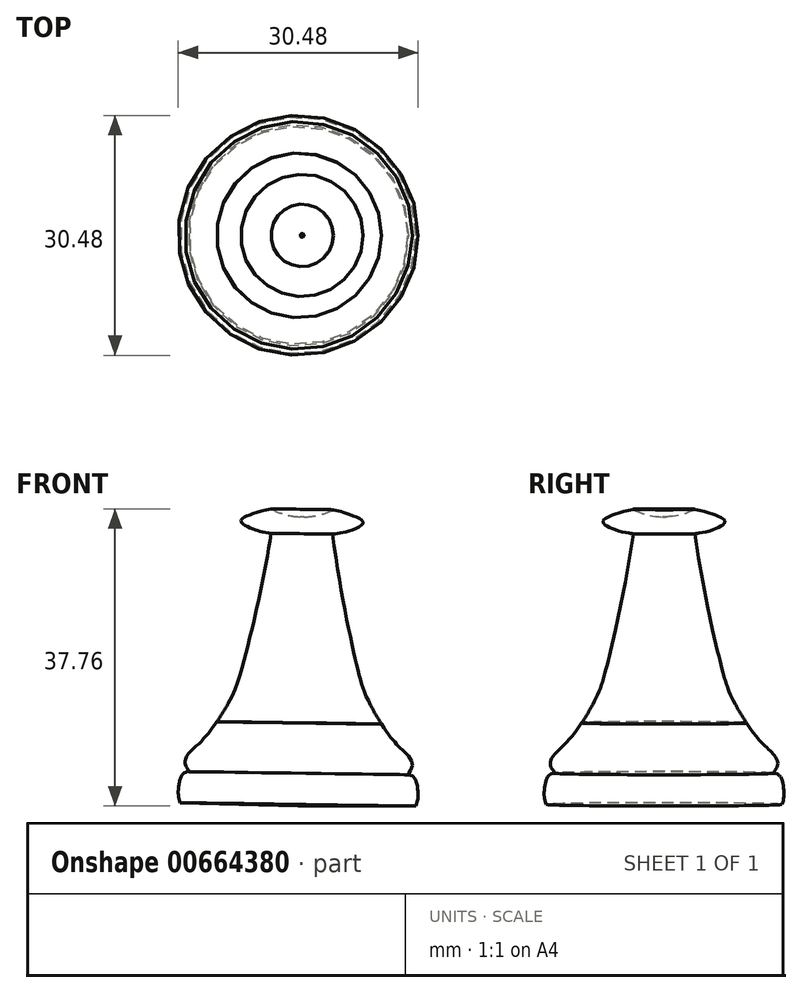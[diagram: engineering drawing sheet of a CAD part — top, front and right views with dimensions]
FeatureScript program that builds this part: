
annotation { "Feature Type Name" : "Feature", "Feature Type Description" : "" }
export const myFeature = defineFeature(function(context is Context, id is Id, definition is map)
    precondition{}
    {
        {
            var Q0;
            Q0=qCreatedBy(makeId("Front.planeOp"),FACE);
            var sketch = newSketch(context, id + "F0", { "sketchPlane" : qUnion([Q0])});
            skArc(sketch, "E0", {"start": v(-3.17, 17.76) * mm, "mid": v(1.07, 26.98) * mm, "end": v(-6.9, 33.26) * mm});
            skFitSpline(sketch, "E1", {"points": [v(-3.17, 17.76) * mm, v(-1.24, 17.2) * mm, v(0.61, 16.13) * mm, v(-1.32, 15.01) * mm, v(-3.28, 14.66) * mm], "startDerivative": vector(7.23, -1.58) * mm, "endDerivative": vector(-7.42, -0.73) * mm});
            skFitSpline(sketch, "E2", {"points": [v(6.36, -15.9) * mm, v(7.55, -17.9) * mm, v(7.34, -19.89) * mm], "startDerivative": vector(6.2, -0.64) * mm, "endDerivative": vector(-2.05, -6.68) * mm});
            skLineSegment(sketch, "E3", {"start": v(-7.66, -19.89) * mm, "end": v(7.34, -19.89) * mm});
            skLineSegment(sketch, "E4", {"start": v(-6.9, 33.26) * mm, "end": v(-7.66, -19.89) * mm});
            skFitSpline(sketch, "E5", {"points": [v(6.36, -15.9) * mm, v(6.33, -15.95) * mm, v(6.82, -14.97) * mm, v(5.9, -13.07) * mm, v(4.06, -11.07) * mm, v(1.14, -6.22) * mm, v(-0.14, -2.21) * mm, v(-3.28, 14.66) * mm], "startDerivative": vector(21.6, 3.05) * mm, "endDerivative": vector(-8.8, 68.35) * mm});
            skFitSpline(sketch, "E6", {"points": [v(2.96, -9.48) * mm, v(2.93, -9.15) * mm, v(2.85, -8.77) * mm, v(2.3, -8.2) * mm, v(1.57, -7.08) * mm], "startDerivative": vector(-0.97, 1.1) * mm, "endDerivative": vector(-0.91, 1.4) * mm});
            skSolve(sketch);
        }
        {
            var Q0;
            Q0=makeQuery(id+"F0.imprint","IMPRINT",FACE,{"disambiguationData":[TD([[makeQuery(id+"F0.imprint","IMPRINT",EDGE,{"derivedFrom":sQuery(id+"F0.wireOp",EDGE,"E0")}),1.0]])]});
            var Q1;
            Q1=sQuery(id+"F0.wireOp",EDGE,"E4");
            revolve(context, id + "F1", {"entities" : qUnion([Q0]), "axis" : qUnion([Q1]), "revolveType" : RevolveType.FULL});
        }
    });
